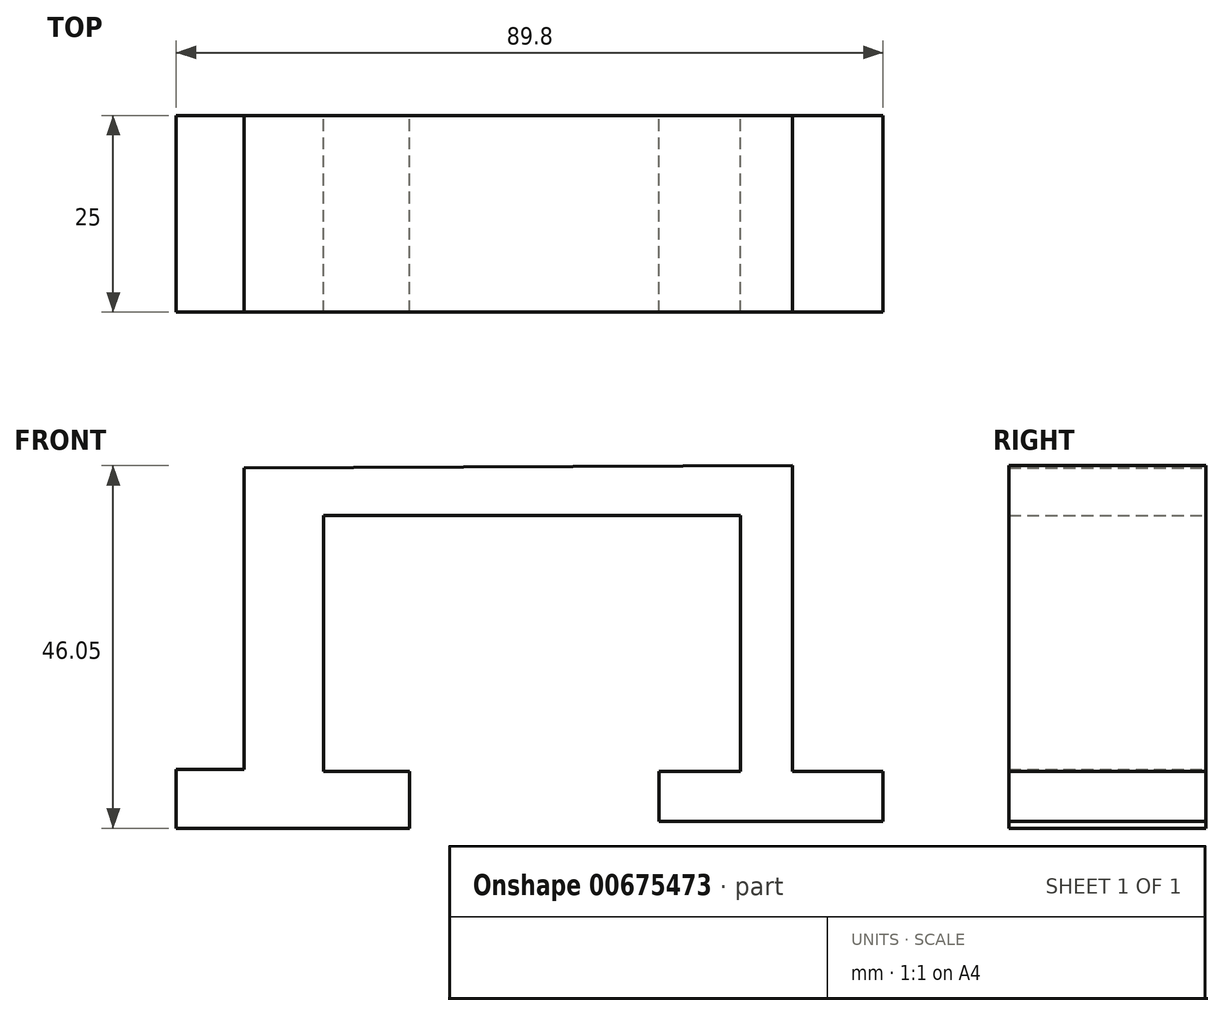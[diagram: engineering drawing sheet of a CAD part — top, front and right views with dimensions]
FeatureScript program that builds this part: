
annotation { "Feature Type Name" : "Feature", "Feature Type Description" : "" }
export const myFeature = defineFeature(function(context is Context, id is Id, definition is map)
    precondition{}
    {
        {
            var Q0;
            Q0=qCreatedBy(makeId("Front.planeOp"),FACE);
            var sketch = newSketch(context, id + "F0", { "sketchPlane" : qUnion([Q0])});
            skLineSegment(sketch, "E0", {"start": v(-37.27, -17.99) * mm, "end": v(-45.9, -17.99) * mm});
            skLineSegment(sketch, "E1", {"start": v(-45.9, -17.99) * mm, "end": v(-45.9, -25.47) * mm});
            skLineSegment(sketch, "E2", {"start": v(-45.9, -25.47) * mm, "end": v(-16.26, -25.47) * mm});
            skLineSegment(sketch, "E3", {"start": v(-16.26, -25.47) * mm, "end": v(-16.26, -18.28) * mm});
            skLineSegment(sketch, "E4", {"start": v(-16.26, -18.28) * mm, "end": v(-27.2, -18.28) * mm});
            skLineSegment(sketch, "E5", {"start": v(-27.2, -18.28) * mm, "end": v(-27.2, 14.25) * mm});
            skLineSegment(sketch, "E6", {"start": v(-27.2, 14.25) * mm, "end": v(25.76, 14.25) * mm});
            skLineSegment(sketch, "E7", {"start": v(25.76, 14.25) * mm, "end": v(25.76, -18.28) * mm});
            skLineSegment(sketch, "E8", {"start": v(25.76, -18.28) * mm, "end": v(15.4, -18.28) * mm});
            skLineSegment(sketch, "E9", {"start": v(15.4, -18.28) * mm, "end": v(15.4, -24.6) * mm});
            skLineSegment(sketch, "E10", {"start": v(15.4, -24.6) * mm, "end": v(43.9, -24.6) * mm});
            skLineSegment(sketch, "E11", {"start": v(43.9, -24.6) * mm, "end": v(43.9, -18.28) * mm});
            skLineSegment(sketch, "E12", {"start": v(43.9, -18.28) * mm, "end": v(32.38, -18.28) * mm});
            skLineSegment(sketch, "E13", {"start": v(32.38, -18.28) * mm, "end": v(32.38, 20.58) * mm});
            skLineSegment(sketch, "E14", {"start": v(-37.27, -17.99) * mm, "end": v(-37.27, 20.3) * mm});
            skLineSegment(sketch, "E15", {"start": v(32.38, 20.58) * mm, "end": v(-37.27, 20.3) * mm});
            skSolve(sketch);
        }
        {
            var Q0;
            Q0 = qSketchRegion(id + "F0", true);
            extrude(context, id + "F1", {"entities" : qUnion([Q0]), "depth" : 25 * mm, "offsetDistance" : 25 * mm});
        }
    });
